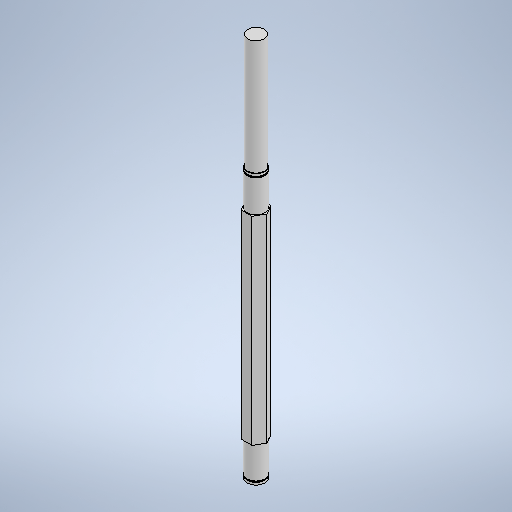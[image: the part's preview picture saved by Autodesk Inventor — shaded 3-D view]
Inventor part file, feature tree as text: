
AUTODESK INVENTOR PART (.ipt)
format: ipt  version: 2025.1 (Build 291241020, 241B)  size: 305,152 bytes
history: native  units: mm
features: sketch x3, extrude x2, revolve x1, plane x1, projected_geometry x1
ambient origin geometry x8: Origin, YZ Plane, XZ Plane, XY Plane, X Axis, Y Axis, Z Axis, Center Point
bodies: Solid1 (feature_tree)
feature tree (8):
  extrude  "Extrusion1"  Depth=334.0mm TaperAngle=0.0deg
  revolve  "Revolution1"  [1 undecoded]
  plane  "Work Plane1"
  extrude  "Extrusion3"  Depth=4.0mm
  sketch  "Sketch1"  dims[d0=32.0mm d1=334.0mm d2=0.0mm]
  sketch  "Sketch3"  dims[d8=30.0mm d9=227.0mm]
  sketch  "Sketch4"  dims[d10=420.0mm d12=28.0mm d13=360.0deg d14=4.0mm d15=2.0mm d16=26.0mm d17=2.0mm d18=4.0mm d19=28.0mm d20=227.0mm d21=2.0mm d22=4.0mm d23=28.0mm d24=8.0mm d25=10.0mm d26=120.0mm d27=4.0mm d28=0.0mm]
  projected_geometry  "Projected Loop1"
note: 1 required parameter value undecoded (feature->parameter linkage not recoverable at this tier; creation-order binding heuristic only, values carry confidence <= 0.55)
